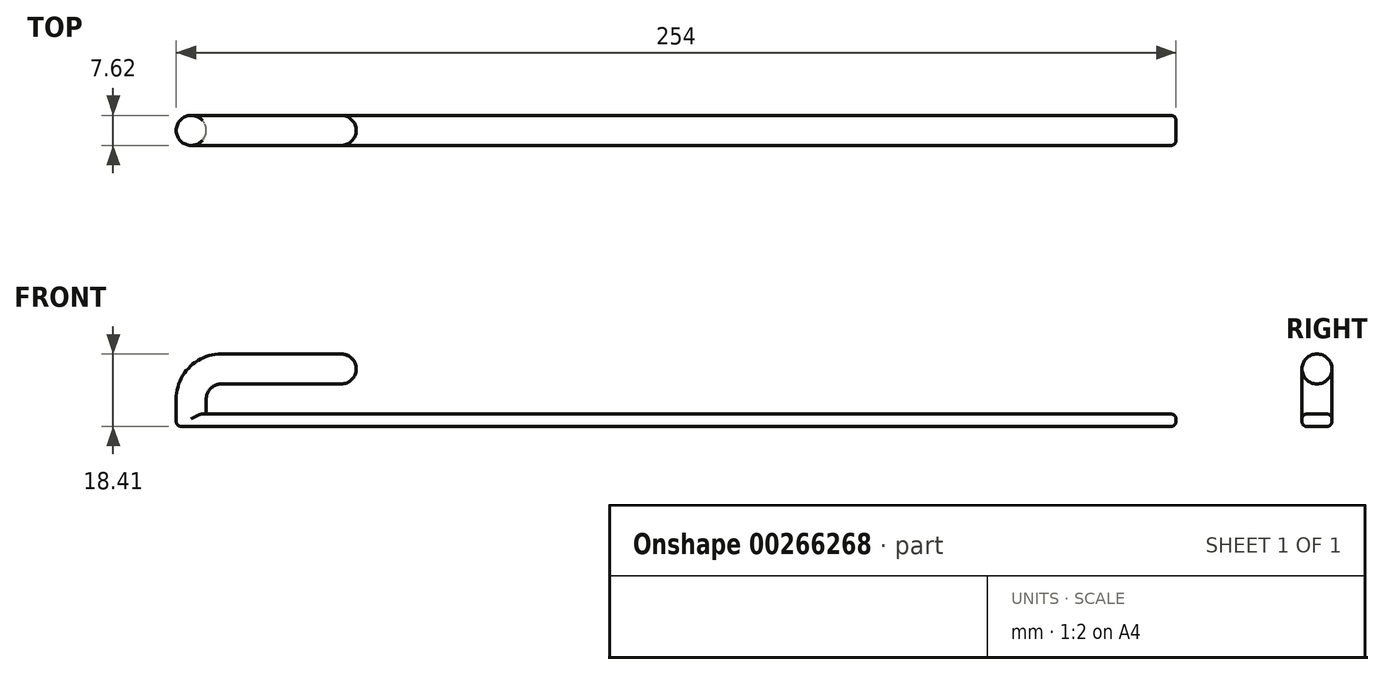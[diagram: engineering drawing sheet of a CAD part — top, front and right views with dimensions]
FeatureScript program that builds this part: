
annotation { "Feature Type Name" : "Feature", "Feature Type Description" : "" }
export const myFeature = defineFeature(function(context is Context, id is Id, definition is map)
    precondition{}
    {
        {
            var Q0;
            Q0=qCreatedBy(makeId("Front.planeOp"),FACE);
            var sketch = newSketch(context, id + "F0", { "sketchPlane" : qUnion([Q0])});
            skLineSegment(sketch, "E0.bottom", {"start": v(-111.6, 37.2) * mm, "end": v(134.77, 37.2) * mm});
            skLineSegment(sketch, "E0.top", {"start": v(-119.23, 34.03) * mm, "end": v(134.77, 34.03) * mm});
            skLineSegment(sketch, "E0.left", {"start": v(-119.23, 37.2) * mm, "end": v(-119.23, 34.03) * mm});
            skLineSegment(sketch, "E0.right", {"start": v(134.77, 37.2) * mm, "end": v(134.77, 34.03) * mm});
            skLineSegment(sketch, "E1.left", {"start": v(-119.23, 37.2) * mm, "end": v(-119.23, 44.82) * mm});
            skLineSegment(sketch, "E1.right", {"start": v(-111.6, 37.2) * mm, "end": v(-111.6, 41.01) * mm});
            skLineSegment(sketch, "E2.bottom", {"start": v(-107.8, 44.82) * mm, "end": v(-73.5, 44.82) * mm});
            skLineSegment(sketch, "E2.top", {"start": v(-107.8, 52.44) * mm, "end": v(-73.5, 52.44) * mm});
            skLineSegment(sketch, "E2.left", {"start": v(-119.23, 41.01) * mm, "end": v(-119.23, 44.82) * mm});
            skLineSegment(sketch, "E2.right", {"start": v(-73.5, 44.82) * mm, "end": v(-73.5, 52.44) * mm});
            skPoint(sketch, "E3.visualSharp", {"position": v(-119.23, 52.44) * mm});
            skArc(sketch, "E3.filletArc", {"start": v(-107.8, 52.44) * mm, "mid": v(-115.88, 49.1) * mm, "end": v(-119.23, 41.01) * mm});
            skPoint(sketch, "E4.visualSharp", {"position": v(-111.6, 44.82) * mm});
            skArc(sketch, "E4.filletArc", {"start": v(-107.8, 44.82) * mm, "mid": v(-110.5, 43.7) * mm, "end": v(-111.6, 41.01) * mm});
            skSolve(sketch);
        }
        {
            var Q0;
            Q0=makeQuery(id+"F0.imprint","IMPRINT",FACE,{"disambiguationData":[TD([[makeQuery(id+"F0.imprint","IMPRINT",EDGE,{"derivedFrom":sQuery(id+"F0.wireOp",EDGE,"E0.bottom")}),-1.0]])]});
            extrude(context, id + "F1", {"entities" : qUnion([Q0]), "depth" : 7.62 * mm});
        }
        {
            var Q0;
            Q0=makeQuery(id+"F1.opExtrude","CAP_EDGE",EDGE,{"disambiguationData":[OSD([sQuery(id+"F0.wireOp",EDGE,"E2.top")])],"isStart":false});
            var Q1;
            Q1=makeQuery(id+"F1.opExtrude","CAP_EDGE",EDGE,{"disambiguationData":[OSD([sQuery(id+"F0.wireOp",EDGE,"E2.bottom")])],"isStart":false});
            var Q2;
            Q2=makeQuery(id+"F1.opExtrude","CAP_EDGE",EDGE,{"disambiguationData":[OSD([sQuery(id+"F0.wireOp",EDGE,"E2.bottom")])],"isStart":true});
            var Q3;
            Q3=makeQuery(id+"F1.opExtrude","CAP_EDGE",EDGE,{"disambiguationData":[OSD([sQuery(id+"F0.wireOp",EDGE,"E2.top")])],"isStart":true});
            fillet(context, id + "F2", {"entities" : qUnion([Q0, Q1, Q2, Q3]), "radius" : 3.8 * mm, "tangentPropagation" : true, "allowEdgeOverflow" : false});
        }
        {
            var Q0;
            Q0=makeQuery(id+"F1.opExtrude","SWEPT_EDGE",EDGE,{"disambiguationData":[OSD([sQuery(id+"F0.wireOp",EDGE,"E2.top"),sQuery(id+"F0.wireOp",EDGE,"E2.right")])]});
            var Q1;
            Q1=makeQuery(id+"F2.opFillet","BLEND_EDGE",EDGE,{"blendedFrom":[makeQuery(id+"F1.opExtrude","CAP_EDGE",EDGE,{"disambiguationData":[OSD([sQuery(id+"F0.wireOp",EDGE,"E2.top")])],"isStart":true}),makeQuery(id+"F1.opExtrude","SWEPT_FACE",FACE,{"disambiguationData":[OSD([sQuery(id+"F0.wireOp",EDGE,"E2.right")])]})],"blendedInto":[makeQuery(id+"F1.opExtrude","SWEPT_FACE",FACE,{"disambiguationData":[OSD([sQuery(id+"F0.wireOp",EDGE,"E2.right")])]})]});
            var Q2;
            Q2=makeQuery(id+"F1.opExtrude","CAP_EDGE",EDGE,{"disambiguationData":[OSD([sQuery(id+"F0.wireOp",EDGE,"E2.right")])],"isStart":true});
            var Q3;
            Q3=makeQuery(id+"F2.opFillet","BLEND_EDGE",EDGE,{"blendedFrom":[makeQuery(id+"F1.opExtrude","CAP_EDGE",EDGE,{"disambiguationData":[OSD([sQuery(id+"F0.wireOp",EDGE,"E2.bottom")])],"isStart":true}),makeQuery(id+"F1.opExtrude","SWEPT_FACE",FACE,{"disambiguationData":[OSD([sQuery(id+"F0.wireOp",EDGE,"E2.right")])]})],"blendedInto":[makeQuery(id+"F1.opExtrude","SWEPT_FACE",FACE,{"disambiguationData":[OSD([sQuery(id+"F0.wireOp",EDGE,"E2.right")])]})]});
            var Q4;
            Q4=makeQuery(id+"F1.opExtrude","SWEPT_EDGE",EDGE,{"disambiguationData":[OSD([sQuery(id+"F0.wireOp",EDGE,"E2.bottom"),sQuery(id+"F0.wireOp",EDGE,"E2.right")])]});
            var Q5;
            Q5=makeQuery(id+"F2.opFillet","BLEND_EDGE",EDGE,{"blendedFrom":[makeQuery(id+"F1.opExtrude","CAP_EDGE",EDGE,{"disambiguationData":[OSD([sQuery(id+"F0.wireOp",EDGE,"E2.bottom")])],"isStart":false}),makeQuery(id+"F1.opExtrude","SWEPT_FACE",FACE,{"disambiguationData":[OSD([sQuery(id+"F0.wireOp",EDGE,"E2.right")])]})],"blendedInto":[makeQuery(id+"F1.opExtrude","SWEPT_FACE",FACE,{"disambiguationData":[OSD([sQuery(id+"F0.wireOp",EDGE,"E2.right")])]})]});
            var Q6;
            Q6=makeQuery(id+"F2.opFillet","BLEND_EDGE",EDGE,{"blendedFrom":[makeQuery(id+"F1.opExtrude","CAP_EDGE",EDGE,{"disambiguationData":[OSD([sQuery(id+"F0.wireOp",EDGE,"E2.top")])],"isStart":false}),makeQuery(id+"F1.opExtrude","SWEPT_FACE",FACE,{"disambiguationData":[OSD([sQuery(id+"F0.wireOp",EDGE,"E2.right")])]})],"blendedInto":[makeQuery(id+"F1.opExtrude","SWEPT_FACE",FACE,{"disambiguationData":[OSD([sQuery(id+"F0.wireOp",EDGE,"E2.right")])]})]});
            var Q7;
            Q7=makeQuery(id+"F1.opExtrude","CAP_EDGE",EDGE,{"disambiguationData":[OSD([sQuery(id+"F0.wireOp",EDGE,"E2.right")])],"isStart":false});
            fillet(context, id + "F3", {"entities" : qUnion([Q0, Q1, Q2, Q3, Q4, Q5, Q6, Q7]), "radius" : 3.8 * mm, "tangentPropagation" : true, "allowEdgeOverflow" : false});
        }
        {
            var Q0;
            Q0=makeQuery(id+"F1.opExtrude","CAP_EDGE",EDGE,{"disambiguationData":[OSD([sQuery(id+"F0.wireOp",EDGE,"E0.bottom")])],"isStart":false});
            var Q1;
            Q1=makeQuery(id+"F1.opExtrude","CAP_EDGE",EDGE,{"disambiguationData":[OSD([sQuery(id+"F0.wireOp",EDGE,"E0.top")])],"isStart":false});
            var Q2;
            Q2=makeQuery(id+"F1.opExtrude","CAP_EDGE",EDGE,{"disambiguationData":[OSD([sQuery(id+"F0.wireOp",EDGE,"E0.bottom")])],"isStart":true});
            var Q3;
            Q3=makeQuery(id+"F1.opExtrude","CAP_EDGE",EDGE,{"disambiguationData":[OSD([sQuery(id+"F0.wireOp",EDGE,"E0.top")])],"isStart":true});
            fillet(context, id + "F4", {"entities" : qUnion([Q0, Q1, Q2, Q3]), "radius" : 1.27 * mm, "tangentPropagation" : true, "allowEdgeOverflow" : false});
        }
        {
            var Q0;
            Q0=makeQuery(id+"F4.opFillet","BLEND_EDGE",EDGE,{"blendedFrom":[makeQuery(id+"F1.opExtrude","CAP_EDGE",EDGE,{"disambiguationData":[OSD([sQuery(id+"F0.wireOp",EDGE,"E0.bottom")])],"isStart":false}),makeQuery(id+"F1.opExtrude","SWEPT_FACE",FACE,{"disambiguationData":[OSD([sQuery(id+"F0.wireOp",EDGE,"E0.right")])]})],"blendedInto":[makeQuery(id+"F1.opExtrude","SWEPT_FACE",FACE,{"disambiguationData":[OSD([sQuery(id+"F0.wireOp",EDGE,"E0.right")])]})]});
            var Q1;
            Q1=makeQuery(id+"F1.opExtrude","CAP_EDGE",EDGE,{"disambiguationData":[OSD([sQuery(id+"F0.wireOp",EDGE,"E0.right")])],"isStart":false});
            var Q2;
            Q2=makeQuery(id+"F4.opFillet","BLEND_EDGE",EDGE,{"blendedFrom":[makeQuery(id+"F1.opExtrude","CAP_EDGE",EDGE,{"disambiguationData":[OSD([sQuery(id+"F0.wireOp",EDGE,"E0.top")])],"isStart":false}),makeQuery(id+"F1.opExtrude","SWEPT_FACE",FACE,{"disambiguationData":[OSD([sQuery(id+"F0.wireOp",EDGE,"E0.right")])]})],"blendedInto":[makeQuery(id+"F1.opExtrude","SWEPT_FACE",FACE,{"disambiguationData":[OSD([sQuery(id+"F0.wireOp",EDGE,"E0.right")])]})]});
            var Q3;
            Q3=makeQuery(id+"F1.opExtrude","SWEPT_EDGE",EDGE,{"disambiguationData":[OSD([sQuery(id+"F0.wireOp",EDGE,"E0.top"),sQuery(id+"F0.wireOp",EDGE,"E0.right")])]});
            var Q4;
            Q4=makeQuery(id+"F4.opFillet","BLEND_EDGE",EDGE,{"blendedFrom":[makeQuery(id+"F1.opExtrude","CAP_EDGE",EDGE,{"disambiguationData":[OSD([sQuery(id+"F0.wireOp",EDGE,"E0.top")])],"isStart":true}),makeQuery(id+"F1.opExtrude","SWEPT_FACE",FACE,{"disambiguationData":[OSD([sQuery(id+"F0.wireOp",EDGE,"E0.right")])]})],"blendedInto":[makeQuery(id+"F1.opExtrude","SWEPT_FACE",FACE,{"disambiguationData":[OSD([sQuery(id+"F0.wireOp",EDGE,"E0.right")])]})]});
            var Q5;
            Q5=makeQuery(id+"F1.opExtrude","CAP_EDGE",EDGE,{"disambiguationData":[OSD([sQuery(id+"F0.wireOp",EDGE,"E0.right")])],"isStart":true});
            var Q6;
            Q6=makeQuery(id+"F1.opExtrude","SWEPT_EDGE",EDGE,{"disambiguationData":[OSD([sQuery(id+"F0.wireOp",EDGE,"E0.bottom"),sQuery(id+"F0.wireOp",EDGE,"E0.right")])]});
            var Q7;
            Q7=makeQuery(id+"F4.opFillet","BLEND_EDGE",EDGE,{"blendedFrom":[makeQuery(id+"F1.opExtrude","CAP_EDGE",EDGE,{"disambiguationData":[OSD([sQuery(id+"F0.wireOp",EDGE,"E0.bottom")])],"isStart":true}),makeQuery(id+"F1.opExtrude","SWEPT_FACE",FACE,{"disambiguationData":[OSD([sQuery(id+"F0.wireOp",EDGE,"E0.right")])]})],"blendedInto":[makeQuery(id+"F1.opExtrude","SWEPT_FACE",FACE,{"disambiguationData":[OSD([sQuery(id+"F0.wireOp",EDGE,"E0.right")])]})]});
            fillet(context, id + "F5", {"entities" : qUnion([Q0, Q1, Q2, Q3, Q4, Q5, Q6, Q7]), "radius" : 1.27 * mm, "tangentPropagation" : true, "allowEdgeOverflow" : false});
        }
    });
